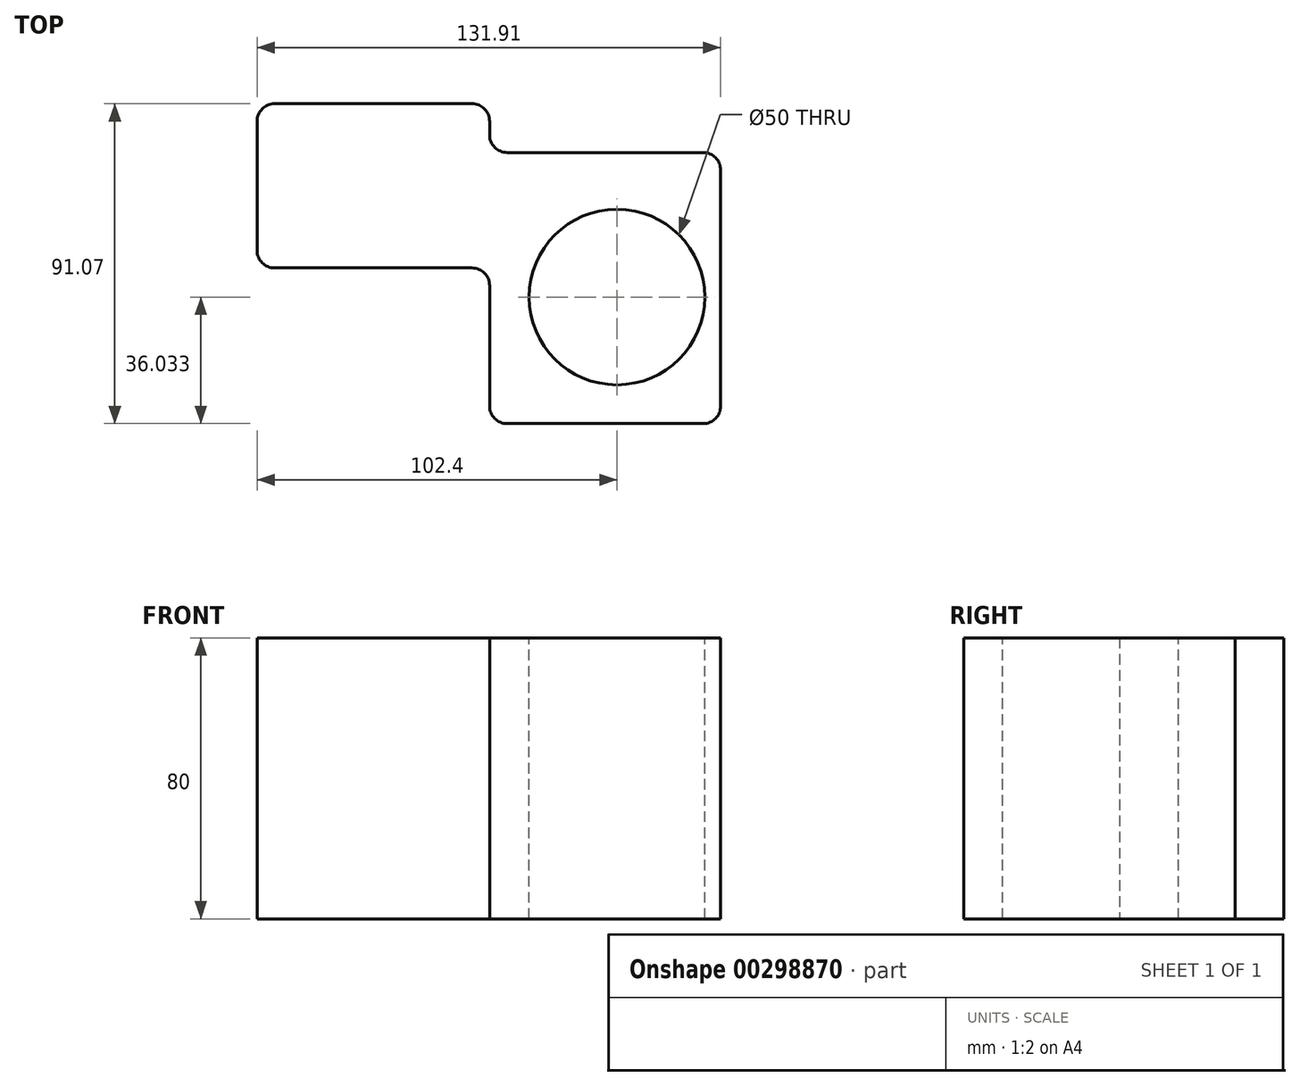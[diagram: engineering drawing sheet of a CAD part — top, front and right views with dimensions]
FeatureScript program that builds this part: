
annotation { "Feature Type Name" : "Feature", "Feature Type Description" : "" }
export const myFeature = defineFeature(function(context is Context, id is Id, definition is map)
    precondition{}
    {
        {
            var Q0;
            Q0=qCreatedBy(makeId("Top.planeOp"),FACE);
            var sketch = newSketch(context, id + "F0", { "sketchPlane" : qUnion([Q0])});
            skLineSegment(sketch, "E0.bottom", {"start": v(9.6, -18.38) * mm, "end": v(-56.56, -18.38) * mm});
            skLineSegment(sketch, "E0.top", {"start": v(9.6, 28.38) * mm, "end": v(-56.56, 28.38) * mm});
            skLineSegment(sketch, "E0.left", {"start": v(9.6, -18.38) * mm, "end": v(9.6, 28.38) * mm});
            skLineSegment(sketch, "E0.right", {"start": v(-56.56, -18.38) * mm, "end": v(-56.56, 28.38) * mm});
            skLineSegment(sketch, "E1.bottom", {"start": v(9.6, 14.5) * mm, "end": v(75.35, 14.5) * mm});
            skLineSegment(sketch, "E1.top", {"start": v(9.6, -62.69) * mm, "end": v(75.35, -62.69) * mm});
            skLineSegment(sketch, "E1.left", {"start": v(9.6, 14.5) * mm, "end": v(9.6, -62.69) * mm});
            skLineSegment(sketch, "E1.right", {"start": v(75.35, 14.5) * mm, "end": v(75.35, -62.69) * mm});
            skSolve(sketch);
        }
        {
            var Q0;
            {var subQ1=sQuery(id+"F0.wireOp",EDGE,"E0.bottom");Q0=makeQuery(id+"F0.imprint","IMPRINT",FACE,{"disambiguationData":[TD([[makeQuery(id+"F0.imprint","IMPRINT",EDGE,{"derivedFrom":subQ1}),-1.0]])]});}
            var Q1;
            {var subQ3=sQuery(id+"F0.wireOp",EDGE,"E1.bottom");Q1=makeQuery(id+"F0.imprint","IMPRINT",FACE,{"disambiguationData":[TD([[makeQuery(id+"F0.imprint","IMPRINT",EDGE,{"derivedFrom":subQ3}),-1.0]])]});}
            extrude(context, id + "F1", {"entities" : qUnion([Q0, Q1]), "depth" : 80 * mm});
        }
        {
            var Q0;
            Q0=makeQuery(id+"F1.opExtrude","SWEPT_EDGE",EDGE,{"disambiguationData":[OSD([sQuery(id+"F0.wireOp",EDGE,"E0.left"),sQuery(id+"F0.wireOp",EDGE,"E1.bottom"),sQuery(id+"F0.wireOp",EDGE,"E1.left")])]});
            var Q1;
            Q1=makeQuery(id+"F1.opExtrude","SWEPT_EDGE",EDGE,{"disambiguationData":[OSD([sQuery(id+"F0.wireOp",EDGE,"E0.bottom"),sQuery(id+"F0.wireOp",EDGE,"E1.left")])]});
            var Q2;
            Q2=makeQuery(id+"F1.opExtrude","SWEPT_EDGE",EDGE,{"disambiguationData":[OSD([sQuery(id+"F0.wireOp",EDGE,"E0.bottom"),sQuery(id+"F0.wireOp",EDGE,"E0.right")])]});
            var Q3;
            Q3=makeQuery(id+"F1.opExtrude","SWEPT_EDGE",EDGE,{"disambiguationData":[OSD([sQuery(id+"F0.wireOp",EDGE,"E0.top"),sQuery(id+"F0.wireOp",EDGE,"E0.right")])]});
            var Q4;
            Q4=makeQuery(id+"F1.opExtrude","SWEPT_EDGE",EDGE,{"disambiguationData":[OSD([sQuery(id+"F0.wireOp",EDGE,"E0.top"),sQuery(id+"F0.wireOp",EDGE,"E0.left")])]});
            var Q5;
            Q5=makeQuery(id+"F1.opExtrude","SWEPT_EDGE",EDGE,{"disambiguationData":[OSD([sQuery(id+"F0.wireOp",EDGE,"E1.bottom"),sQuery(id+"F0.wireOp",EDGE,"E1.right")])]});
            var Q6;
            Q6=makeQuery(id+"F1.opExtrude","SWEPT_EDGE",EDGE,{"disambiguationData":[OSD([sQuery(id+"F0.wireOp",EDGE,"E1.top"),sQuery(id+"F0.wireOp",EDGE,"E1.right")])]});
            var Q7;
            Q7=makeQuery(id+"F1.opExtrude","SWEPT_EDGE",EDGE,{"disambiguationData":[OSD([sQuery(id+"F0.wireOp",EDGE,"E1.top"),sQuery(id+"F0.wireOp",EDGE,"E1.left")])]});
            fillet(context, id + "F2", {"entities" : qUnion([Q0, Q1, Q2, Q3, Q4, Q5, Q6, Q7]), "radius" : 5 * mm, "tangentPropagation" : true, "allowEdgeOverflow" : false});
        }
        {
            var Q0;
            Q0=makeQuery(id+"F1.opExtrude","CAP_FACE",FACE,{"disambiguationData":[OSD([sQuery(id+"F0.wireOp",EDGE,"E0.bottom"),sQuery(id+"F0.wireOp",EDGE,"E0.top"),sQuery(id+"F0.wireOp",EDGE,"E0.left"),sQuery(id+"F0.wireOp",EDGE,"E0.right"),sQuery(id+"F0.wireOp",EDGE,"E1.bottom"),sQuery(id+"F0.wireOp",EDGE,"E1.top"),sQuery(id+"F0.wireOp",EDGE,"E1.left"),sQuery(id+"F0.wireOp",EDGE,"E1.right")])],"isStart":false});
            var sketch = newSketch(context, id + "F3", { "sketchPlane" : qUnion([Q0])});
            skCircle(sketch, "E2", {"center": v(45.84, -26.66) * mm, "radius": 13.09 * mm});
            skSolve(sketch);
        }
        {
            var Q0;
            Q0=sQuery(id+"F3.wireOp",VERTEX,"E2.center");
            var Q1;
            Q1=makeQuery(id+"F1.opExtrude","SWEPT_BODY",BODY,{"disambiguationData":[OSD([sQuery(id+"F0.wireOp",EDGE,"E0.bottom"),sQuery(id+"F0.wireOp",EDGE,"E0.top"),sQuery(id+"F0.wireOp",EDGE,"E0.left"),sQuery(id+"F0.wireOp",EDGE,"E0.right"),sQuery(id+"F0.wireOp",EDGE,"E1.bottom"),sQuery(id+"F0.wireOp",EDGE,"E1.top"),sQuery(id+"F0.wireOp",EDGE,"E1.left"),sQuery(id+"F0.wireOp",EDGE,"E1.right")])]});
            hole(context, id + "F4", {"style" : HoleStyle.SIMPLE, "endStyle" : HoleEndStyle.THROUGH, "holeDiameter" : 50 * mm, "tappedDepth" : 12 * mm, "tapClearance" : 3, "locations" : qUnion([Q0]), "scope" : qUnion([Q1])});
        }
    });
